FCSTD DOCUMENT  (FreeCAD 0.20R29177 (Git))
Label: KeyboardLabels_Select_Start
License: All rights reserved
LicenseURL: http://en.wikipedia.org/wiki/All_rights_reserved
objects: Sketcher::SketchObject×6
note: 6 computed .brp shape members not serialized (recipe doc carries the construction recipe); baked Part::Feature solids carry a one-line shape summary decoded from their .brp

FEATURE [Sketcher::SketchObject] Sketch  label="A4"
  FullyConstrained = true
  MapMode = 5
  Support = -> [XY_Plane]
  sketch-geometry (4):
    g0: LineSegment StartX=0 StartY=0 StartZ=0 EndX=297 EndY=0 EndZ=0
    g1: LineSegment StartX=297 StartY=0 StartZ=0 EndX=297 EndY=210 EndZ=0
    g2: LineSegment StartX=297 StartY=210 StartZ=0 EndX=0 EndY=210 EndZ=0
    g3: LineSegment StartX=0 StartY=210 StartZ=0 EndX=0 EndY=0 EndZ=0
  constraints (11):
    c: Coincident(g0,g1)
    c: Coincident(g1,g2)
    c: Coincident(g2,g3)
    c: Coincident(g3,g0)
    c: Horizontal(g0)
    c: Horizontal(g2)
    c: Vertical(g1)
    c: Vertical(g3)
    c: Coincident(g0,g-1)
    c: DistanceX(g0,g0) = 297
    c: DistanceY(g3,g3) = 210
FEATURE [Sketcher::SketchObject] Sketch003  label="A005"
  FullyConstrained = true
  MapMode = 5
  Support = -> [XY_Plane002]
  sketch-geometry (4):
    g0: LineSegment StartX=0 StartY=0 StartZ=0 EndX=297 EndY=0 EndZ=0
    g1: LineSegment StartX=297 StartY=0 StartZ=0 EndX=297 EndY=210 EndZ=0
    g2: LineSegment StartX=297 StartY=210 StartZ=0 EndX=0 EndY=210 EndZ=0
    g3: LineSegment StartX=0 StartY=210 StartZ=0 EndX=0 EndY=0 EndZ=0
  constraints (11):
    c: Coincident(g0,g1)
    c: Coincident(g1,g2)
    c: Coincident(g2,g3)
    c: Coincident(g3,g0)
    c: Horizontal(g0)
    c: Horizontal(g2)
    c: Vertical(g1)
    c: Vertical(g3)
    c: Coincident(g0,g-1)
    c: DistanceX(g0,g0) = 297
    c: DistanceY(g3,g3) = 210
FEATURE [Sketcher::SketchObject] Sketch004  label="psp_symbols"
  ExternalGeometry = -> [Sketch003]
  FullyConstrained = false
  MapMode = 5
  Support = -> [XY_Plane003]
  sketch-geometry (9):
    g0: ArcOfCircle CenterX=30.0401 CenterY=30.1519 CenterZ=0 NormalX=0 NormalY=0 NormalZ=1 AngleXU=0 Radius=11 StartAngle=0.4297 EndAngle=5.85349
    g1: ArcOfCircle CenterX=50.0401 CenterY=30.1519 CenterZ=0 NormalX=0 NormalY=0 NormalZ=1 AngleXU=0 Radius=11 StartAngle=0.4297 EndAngle=2.71189
    g2: ArcOfCircle CenterX=70.0401 CenterY=30.1519 CenterZ=0 NormalX=0 NormalY=0 NormalZ=1 AngleXU=0 Radius=11 StartAngle=0.4297 EndAngle=2.71189
    g3: ArcOfCircle CenterX=90.0401 CenterY=30.1519 CenterZ=0 NormalX=0 NormalY=0 NormalZ=1 AngleXU=0 Radius=11 StartAngle=3.57129 EndAngle=8.99508
    g4: LineSegment StartX=30.0401 StartY=30.1519 StartZ=0 EndX=50.0401 EndY=30.1519 EndZ=0
    g5: LineSegment StartX=50.0401 StartY=30.1519 StartZ=0 EndX=70.0401 EndY=30.1519 EndZ=0
    g6: LineSegment StartX=70.0401 StartY=30.1519 StartZ=0 EndX=90.0401 EndY=30.1519 EndZ=0
    g7: ArcOfCircle CenterX=70.0401 CenterY=30.1519 CenterZ=0 NormalX=0 NormalY=0 NormalZ=1 AngleXU=0 Radius=11 StartAngle=3.57129 EndAngle=5.85349
    g8: ArcOfCircle CenterX=50.0401 CenterY=30.1519 CenterZ=0 NormalX=0 NormalY=0 NormalZ=1 AngleXU=0 Radius=11 StartAngle=3.57129 EndAngle=5.85349
  constraints (28):
    c: Diameter(g0) = 22
    c: Coincident(g4,g0)
    c: Coincident(g4,g1)
    c: Horizontal(g4)
    c: Coincident(g5,g1)
    c: Coincident(g5,g2)
    c: Coincident(g6,g2)
    c: Coincident(g6,g3)
    c: Horizontal(g6)
    c: Horizontal(g5)
    c: Equal(g5,g4)
    c: Equal(g4,g6)
    c: Equal(g0,g1)
    c: Equal(g1,g2)
    c: Equal(g2,g3)
    c: DistanceX(g4,g4) = 20
    c: Coincident(g3,g2)
    c: Coincident(g3,g7)
    c: PointOnObject(g8,g2)
    c: Equal(g2,g7)
    c: Coincident(g2,g1)
    c: Coincident(g2,g7)
    c: PointOnObject(g7,g1)
    c: PointOnObject(g0,g1)
    c: Equal(g1,g8)
    c: Coincident(g1,g0)
    c: Coincident(g1,g8)
    c: PointOnObject(g8,g0)
FEATURE [Sketcher::SketchObject] Sketch005  label="A006"
  FullyConstrained = true
  MapMode = 5
  Support = -> [XY_Plane004]
  sketch-geometry (4):
    g0: LineSegment StartX=0 StartY=0 StartZ=0 EndX=297 EndY=0 EndZ=0
    g1: LineSegment StartX=297 StartY=0 StartZ=0 EndX=297 EndY=210 EndZ=0
    g2: LineSegment StartX=297 StartY=210 StartZ=0 EndX=0 EndY=210 EndZ=0
    g3: LineSegment StartX=0 StartY=210 StartZ=0 EndX=0 EndY=0 EndZ=0
  constraints (11):
    c: Coincident(g0,g1)
    c: Coincident(g1,g2)
    c: Coincident(g2,g3)
    c: Coincident(g3,g0)
    c: Horizontal(g0)
    c: Horizontal(g2)
    c: Vertical(g1)
    c: Vertical(g3)
    c: Coincident(g0,g-1)
    c: DistanceX(g0,g0) = 297
    c: DistanceY(g3,g3) = 210
FEATURE [Sketcher::SketchObject] Sketch006  label="psp_symbols_outline"
  ExternalGeometry = -> [Sketch005,Sketch004]
  FullyConstrained = false
  MapMode = 5
  Support = -> [XY_Plane005]
  sketch-geometry (6):
    g0: ArcOfCircle CenterX=30.0401 CenterY=30.1519 CenterZ=0 NormalX=0 NormalY=0 NormalZ=1 AngleXU=0 Radius=12.6225 StartAngle=0.656332 EndAngle=5.62685
    g1: ArcOfCircle CenterX=50.0401 CenterY=30.1519 CenterZ=0 NormalX=0 NormalY=0 NormalZ=1 AngleXU=0 Radius=12.6225 StartAngle=0.656332 EndAngle=2.48526
    g2: ArcOfCircle CenterX=70.0401 CenterY=30.1519 CenterZ=0 NormalX=0 NormalY=0 NormalZ=1 AngleXU=0 Radius=12.6225 StartAngle=0.656332 EndAngle=2.48526
    g3: ArcOfCircle CenterX=90.0401 CenterY=30.1519 CenterZ=0 NormalX=0 NormalY=0 NormalZ=1 AngleXU=0 Radius=12.6225 StartAngle=3.79792 EndAngle=8.76845
    g4: ArcOfCircle CenterX=70.0401 CenterY=30.1519 CenterZ=0 NormalX=0 NormalY=0 NormalZ=1 AngleXU=0 Radius=12.6225 StartAngle=3.79792 EndAngle=5.62685
    g5: ArcOfCircle CenterX=50.0401 CenterY=30.1519 CenterZ=0 NormalX=0 NormalY=0 NormalZ=1 AngleXU=0 Radius=12.6225 StartAngle=3.79792 EndAngle=5.62685
  constraints (17):
    c: Coincident(g0,g-4)
    c: Coincident(g1,g-9)
    c: Coincident(g2,g-8)
    c: Coincident(g3,g-7)
    c: Equal(g0,g1)
    c: Equal(g1,g2)
    c: Equal(g2,g3)
    c: Equal(g2,g4)
    c: Coincident(g2,g4)
    c: Equal(g1,g5)
    c: Coincident(g1,g5)
    c: Coincident(g3,g4)
    c: Coincident(g3,g2)
    c: Coincident(g2,g1)
    c: Coincident(g4,g5)
    c: Coincident(g5,g0)
    c: Coincident(g0,g1)
FEATURE [Sketcher::SketchObject] Sketch007  label="Symbols_Start_Play"
  FullyConstrained = false
  MapMode = 2
  Support = -> [Sketch003]
  sketch-geometry (29):
    g0: LineSegment StartX=34.5595 StartY=29.9962 StartZ=0 EndX=24.4802 EndY=35.8155 EndZ=0
    g1: LineSegment StartX=24.4802 StartY=35.8155 StartZ=0 EndX=24.4802 EndY=24.1769 EndZ=0
    g2: LineSegment StartX=24.4802 StartY=24.1769 StartZ=0 EndX=34.5595 EndY=29.9962 EndZ=0
    g3: Circle CenterX=27.8399 CenterY=29.9962 CenterZ=0 NormalX=0 NormalY=0 NormalZ=1 AngleXU=0 Radius=6.71955
    g4: LineSegment StartX=76.7731 StartY=30.2239 StartZ=0 EndX=66.6938 EndY=36.0432 EndZ=0
    g5: LineSegment StartX=66.6938 StartY=36.0432 StartZ=0 EndX=66.6938 EndY=24.4046 EndZ=0
    g6: LineSegment StartX=66.6938 StartY=24.4046 StartZ=0 EndX=76.7731 EndY=30.2239 EndZ=0
    g7: Circle CenterX=70.0536 CenterY=30.2239 CenterZ=0 NormalX=0 NormalY=0 NormalZ=1 AngleXU=0 Radius=6.71955
    g8: LineSegment StartX=34.5595 StartY=35.8155 StartZ=0 EndX=37.486 EndY=35.8155 EndZ=0
    g9: LineSegment StartX=37.486 StartY=35.8155 StartZ=0 EndX=37.486 EndY=24.1769 EndZ=0
    g10: LineSegment StartX=37.486 StartY=24.1769 StartZ=0 EndX=34.5595 EndY=24.1769 EndZ=0
    g11: LineSegment StartX=34.5595 StartY=24.1769 StartZ=0 EndX=34.5595 EndY=35.8155 EndZ=0
    g12: LineSegment StartX=46.9918 StartY=24.7645 StartZ=0 EndX=54.4388 EndY=24.7645 EndZ=0
    g13: LineSegment StartX=54.4388 StartY=24.7645 StartZ=0 EndX=54.4388 EndY=31.6369 EndZ=0
    g14: LineSegment StartX=54.4388 StartY=31.6369 StartZ=0 EndX=57.3624 EndY=31.6369 EndZ=0
    g15: LineSegment StartX=57.3624 StartY=31.6369 StartZ=0 EndX=50.7153 EndY=36.5427 EndZ=0
    g16: LineSegment StartX=50.7153 StartY=36.5427 StartZ=0 EndX=44.0682 EndY=31.6369 EndZ=0
    g17: LineSegment StartX=44.0682 StartY=31.6369 StartZ=0 EndX=46.9918 EndY=31.6369 EndZ=0
    g18: LineSegment StartX=46.9918 StartY=31.6369 StartZ=0 EndX=46.9918 EndY=24.7645 EndZ=0
    g19: ArcOfCircle CenterX=90.247 CenterY=30.0628 CenterZ=0 NormalX=0 NormalY=0 NormalZ=1 AngleXU=0 Radius=6.27453 StartAngle=1.92984 EndAngle=7.49494
    g20: LineSegment StartX=88.0423 StartY=35.9373 StartZ=0 EndX=88.0423 EndY=30.0628 EndZ=0
    g21: LineSegment StartX=88.0423 StartY=30.0628 StartZ=0 EndX=90.247 EndY=30.0628 EndZ=0
    g22: LineSegment StartX=90.247 StartY=30.0628 StartZ=0 EndX=92.4518 EndY=30.0628 EndZ=0
    g23: LineSegment StartX=92.4518 StartY=30.0628 StartZ=0 EndX=92.4518 EndY=35.9373 EndZ=0
    g24: LineSegment StartX=89.1295 StartY=38.7234 StartZ=0 EndX=91.3646 EndY=38.7234 EndZ=0
    g25: LineSegment StartX=91.3646 StartY=38.7234 StartZ=0 EndX=91.3646 EndY=31.2258 EndZ=0
    g26: LineSegment StartX=89.1295 StartY=31.2258 StartZ=0 EndX=89.1295 EndY=38.7234 EndZ=0
    g27: LineSegment StartX=89.1295 StartY=31.2258 StartZ=0 EndX=90.247 EndY=31.2258 EndZ=0
    g28: LineSegment StartX=90.247 StartY=31.2258 StartZ=0 EndX=91.3646 EndY=31.2258 EndZ=0
  constraints (68):
    c: Coincident(g0,g1)
    c: Coincident(g1,g2)
    c: Coincident(g2,g0)
    c: Equal(g0,g1)
    c: Equal(g0,g2)
    c: PointOnObject(g0,g3)
    c: PointOnObject(g1,g3)
    c: PointOnObject(g2,g3)
    c: Vertical(g1)
    c: Coincident(g4,g5)
    c: Coincident(g5,g6)
    c: Coincident(g6,g4)
    c: Equal(g4,g5)
    c: Equal(g4,g6)
    c: PointOnObject(g4,g7)
    c: PointOnObject(g5,g7)
    c: PointOnObject(g6,g7)
    c: Equal(g5,g1)
    c: Vertical(g5)
    c: Coincident(g8,g9)
    c: Coincident(g9,g10)
    c: Coincident(g10,g11)
    c: Coincident(g11,g8)
    c: Horizontal(g8)
    c: Horizontal(g10)
    c: Vertical(g9)
    c: Vertical(g11)
    c: Horizontal(g10,g1)
    c: Horizontal(g8,g0)
    c: Horizontal(g12)
    c: Coincident(g12,g13)
    c: Vertical(g13)
    c: Coincident(g13,g14)
    c: Coincident(g14,g15)
    c: Coincident(g15,g16)
    c: Coincident(g16,g17)
    c: Coincident(g17,g18)
    c: Coincident(g18,g12)
    c: Vertical(g18)
    c: Horizontal(g17)
    c: Horizontal(g14)
    c: Horizontal(g13,g17)
    c: Equal(g14,g17)
    c: Equal(g15,g16)
    c: Vertical(g20)
    c: Coincident(g21,g20)
    c: Coincident(g21,g19)
    c: Coincident(g22,g19)
    c: Horizontal(g22)
    c: Coincident(g23,g22)
    c: Vertical(g23)
    c: Coincident(g19,g23)
    c: Coincident(g19,g20)
    c: Coincident(g24,g25)
    c: Coincident(g26,g24)
    c: Horizontal(g24)
    c: Vertical(g25)
    c: Vertical(g26)
    c: Coincident(g27,g26)
    c: Horizontal(g27)
    c: Coincident(g28,g27)
    c: Coincident(g28,g25)
    c: Horizontal(g28)
    c: Vertical(g19,g27)
    c: Horizontal(g21)
    c: PointOnObject(g0,g11)
    c: Horizontal(g19,g19)
    c: Equal(g27,g28)
